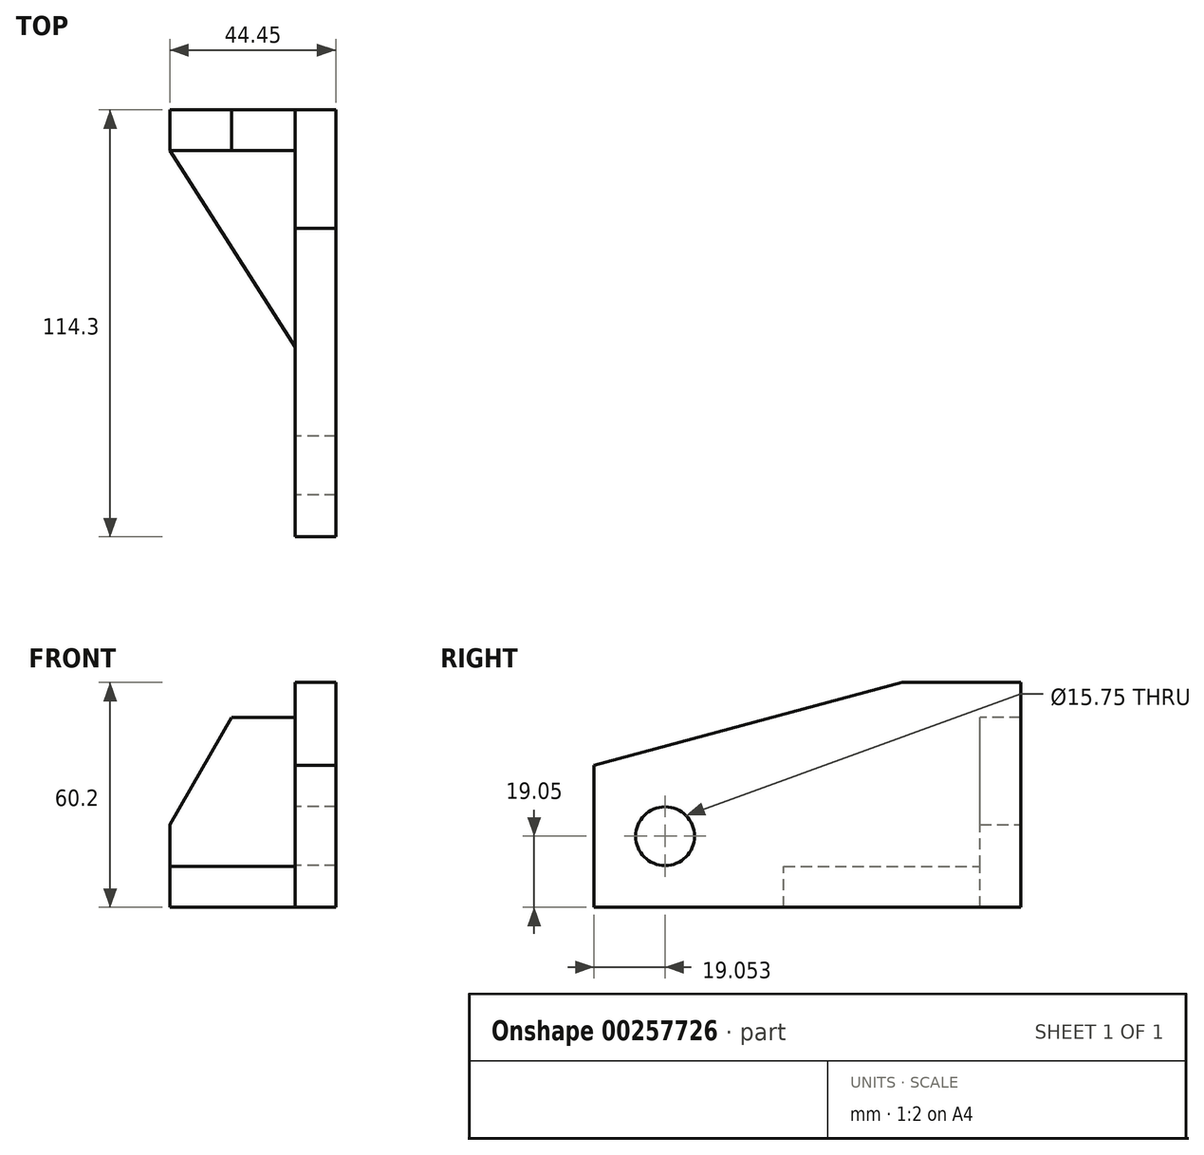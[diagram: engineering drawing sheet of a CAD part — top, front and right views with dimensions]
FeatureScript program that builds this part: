
annotation { "Feature Type Name" : "Feature", "Feature Type Description" : "" }
export const myFeature = defineFeature(function(context is Context, id is Id, definition is map)
    precondition{}
    {
        {
            var Q0;
            Q0=qCreatedBy(makeId("Top.planeOp"),FACE);
            var sketch = newSketch(context, id + "F0", { "sketchPlane" : qUnion([Q0])});
            skLineSegment(sketch, "E0", {"start": v(44.45, 58.35) * mm, "end": v(44.45, -55.95) * mm});
            skLineSegment(sketch, "E1", {"start": v(44.45, -55.95) * mm, "end": v(33.53, -55.95) * mm});
            skLineSegment(sketch, "E2", {"start": v(33.53, -55.95) * mm, "end": v(33.53, 58.35) * mm});
            skLineSegment(sketch, "E3", {"start": v(33.53, 58.35) * mm, "end": v(44.45, 58.35) * mm});
            skLineSegment(sketch, "E4", {"start": v(33.53, 26.6) * mm, "end": v(44.45, 26.6) * mm});
            skSolve(sketch);
        }
        {
            var Q0;
            Q0 = qSketchRegion(id + "F0", true);
            extrude(context, id + "F1", {"entities" : qUnion([Q0]), "depth" : 60.2 * mm});
        }
        {
            var Q0;
            Q0=makeQuery(id+"F1.opExtrude","CAP_EDGE",EDGE,{"disambiguationData":[OSD([sQuery(id+"F0.wireOp",EDGE,"E1")])],"isStart":false});
            chamfer(context, id + "F2", {"entities" : qUnion([Q0]), "chamferType" : ChamferType.OFFSET_ANGLE, "width" : 82.55 * mm, "oppositeDirection" : true, "angle" : 15 * degree, "tangentPropagation" : true});
        }
        {
            var Q0;
            Q0=makeQuery(id+"F1.opExtrude","SWEPT_FACE",FACE,{"disambiguationData":[OSD([sQuery(id+"F0.wireOp",EDGE,"E2")])]});
            var sketch = newSketch(context, id + "F3", { "sketchPlane" : qUnion([Q0])});
            skLineSegment(sketch, "E5.bottom", {"start": v(-58.35, 0) * mm, "end": v(-47.43, 0) * mm});
            skLineSegment(sketch, "E5.top", {"start": v(-58.35, 50.8) * mm, "end": v(-47.43, 50.8) * mm});
            skLineSegment(sketch, "E5.left", {"start": v(-58.35, 0) * mm, "end": v(-58.35, 50.8) * mm});
            skLineSegment(sketch, "E5.right", {"start": v(-47.43, 0) * mm, "end": v(-47.43, 50.8) * mm});
            skLineSegment(sketch, "E6", {"start": v(5.15, 0) * mm, "end": v(5.15, 10.92) * mm});
            skLineSegment(sketch, "E7", {"start": v(5.15, 10.92) * mm, "end": v(-47.43, 10.92) * mm});
            skLineSegment(sketch, "E8", {"start": v(55.95, 19.05) * mm, "end": v(36.9, 19.05) * mm, "construction": true});
            skCircle(sketch, "E9", {"center": v(36.9, 19.05) * mm, "radius": 7.87 * mm});
            skSolve(sketch);
        }
        {
            var Q0;
            {var subQ4=sQuery(id+"F3.wireOp",EDGE,"E6");Q0=makeQuery(id+"F3.imprint","IMPRINT",FACE,{"disambiguationData":[TD([[makeQuery(id+"F3.imprint","IMPRINT",EDGE,{"derivedFrom":subQ4}),1.0]])]});}
            extrude(context, id + "F4", {"entities" : qUnion([Q0]), "operationType" : NewBodyOperationType.ADD, "depth" : 33.53 * mm});
        }
        {
            var Q0;
            {var subQ4=sQuery(id+"F3.wireOp",EDGE,"E6");Q0=makeQuery(id+"F3.imprint","IMPRINT",FACE,{"disambiguationData":[TD([[makeQuery(id+"F3.imprint","IMPRINT",EDGE,{"derivedFrom":subQ4}),1.0]])]});}
            extrude(context, id + "F5", {"entities" : qUnion([Q0]), "operationType" : NewBodyOperationType.ADD, "depth" : 33.53 * mm});
        }
        {
            var Q0;
            {var subQ1=sQuery(id+"F3.wireOp",EDGE,"E5.bottom");Q0=makeQuery(id+"F3.imprint","IMPRINT",FACE,{"disambiguationData":[TD([[makeQuery(id+"F3.imprint","IMPRINT",EDGE,{"derivedFrom":subQ1}),-1.0]])]});}
            extrude(context, id + "F6", {"entities" : qUnion([Q0]), "operationType" : NewBodyOperationType.ADD, "depth" : 33.53 * mm});
        }
        {
            var Q0;
            Q0=makeQuery(id+"F6.opExtrude","CAP_EDGE",EDGE,{"disambiguationData":[OSD([sQuery(id+"F3.wireOp",EDGE,"E5.top")])],"isStart":false});
            chamfer(context, id + "F7", {"entities" : qUnion([Q0]), "chamferType" : ChamferType.OFFSET_ANGLE, "width" : 28.7 * mm, "oppositeDirection" : true, "angle" : 30 * degree, "tangentPropagation" : true});
        }
        {
            var Q0;
            Q0=makeQuery(id+"F4.opExtrude","CAP_EDGE",EDGE,{"disambiguationData":[OSD([sQuery(id+"F3.wireOp",EDGE,"E6")])],"isStart":false});
            chamfer(context, id + "F8", {"entities" : qUnion([Q0]), "chamferType" : ChamferType.TWO_OFFSETS, "width1" : 52.58 * mm, "oppositeDirection" : false, "width2" : 33.53 * mm, "tangentPropagation" : true});
        }
        {
            var Q0;
            Q0=makeQuery(id+"F3.imprint","IMPRINT",FACE,{"disambiguationData":[TD([[makeQuery(id+"F3.imprint","IMPRINT",EDGE,{"derivedFrom":sQuery(id+"F3.wireOp",EDGE,"E9")}),1.0]])]});
            var Q1;
            Q1=sQuery(id+"F3.wireOp",EDGE,"E9");
            extrude(context, id + "F9", {"entities" : qUnion([Q0]), "operationType" : NewBodyOperationType.REMOVE, "surfaceEntities" : qUnion([Q1]), "oppositeDirection" : true, "depth" : 50.8 * mm});
        }
    });
